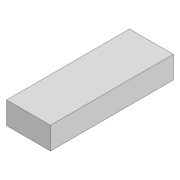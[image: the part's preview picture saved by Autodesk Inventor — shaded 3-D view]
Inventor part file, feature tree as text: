
AUTODESK INVENTOR PART (.ipt)
format: ipt  version: 2022 (Build 260153000, 153)  size: 75,776 bytes
history: native  units: mm
features: extrude x1, sketch x1
ambient origin geometry x8: Origin, YZ Plane, XZ Plane, XY Plane, X Axis, Y Axis, Z Axis, Center Point
bodies: Solid1 (feature_tree)
feature tree (2):
  extrude  "Lipo Body"  Depth=26.0mm
  sketch  "Sketch1"  dims[d0=51.0mm d1=26.0mm d2=143.0mm d3=0.0mm]
